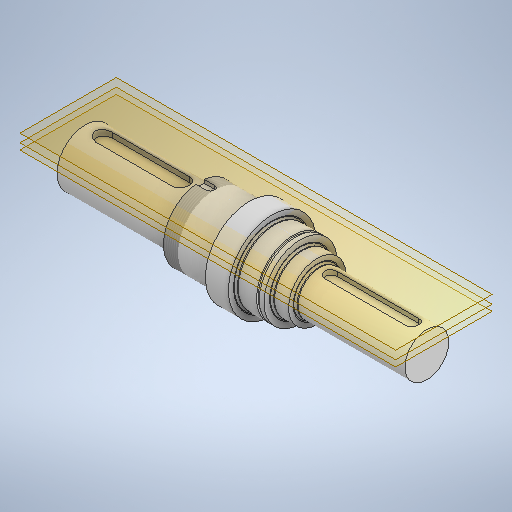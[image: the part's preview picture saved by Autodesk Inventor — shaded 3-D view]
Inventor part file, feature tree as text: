
AUTODESK INVENTOR PART (.ipt)
format: ipt  version: 2025.3 (Build 293356030, 356C)  size: 424,448 bytes
history: native  units: mm
features: sketch x10, revolve x7, plane x3, extrude x3, thread x1
ambient origin geometry x8: Origin, YZ Plane, XZ Plane, XY Plane, X Axis, Y Axis, Z Axis, Center Point
bodies: Body1 (feature_tree)
feature tree (24):
  revolve  "Umdrehung28"
  plane  "Arbeitsebene5"
  extrude  "Extrusion5"  Depth=6.0mm
  revolve  "Umdrehung29"
  revolve  "Umdrehung30"
  thread  "Gewinde1"  [1 undecoded]
  plane  "Arbeitsebene6"
  extrude  "Extrusion6"  TaperAngle=0.0deg  [1 undecoded]
  revolve  "Umdrehung31"
  revolve  "Umdrehung32"
  revolve  "Umdrehung33"
  plane  "Arbeitsebene7"
  extrude  "Extrusion7"  Depth=35.0mm
  revolve  "Umdrehung34"
  sketch  "Skizze32"  dims[d45=0.0mm d46=27.0mm d47=6.0mm d48=0.0mm]
  sketch  "Skizze33"  dims[d49=0.0mm d50=0.0mm]
  sketch  "Skizze34"  dims[d51=14.0mm d52=0.0mm d53=35.0mm]
  sketch  "Skizze35"  dims[d54=3.5mm d55=0.0mm]
  sketch  "Skizze36"  dims[d56=0.0mm]
  sketch  "Skizze37"  dims[d57=0.0mm]
  sketch  "Skizze38"  dims[d58=0.0mm]
  sketch  "Skizze39"  dims[d59=21.0mm]
  sketch  "Skizze40"  dims[d60=5.0mm d61=0.0mm]
  sketch  "Skizze41"  dims[d62=0.0mm]
note: 2 required parameter values undecoded (feature->parameter linkage not recoverable at this tier; creation-order binding heuristic only, values carry confidence <= 0.55)
